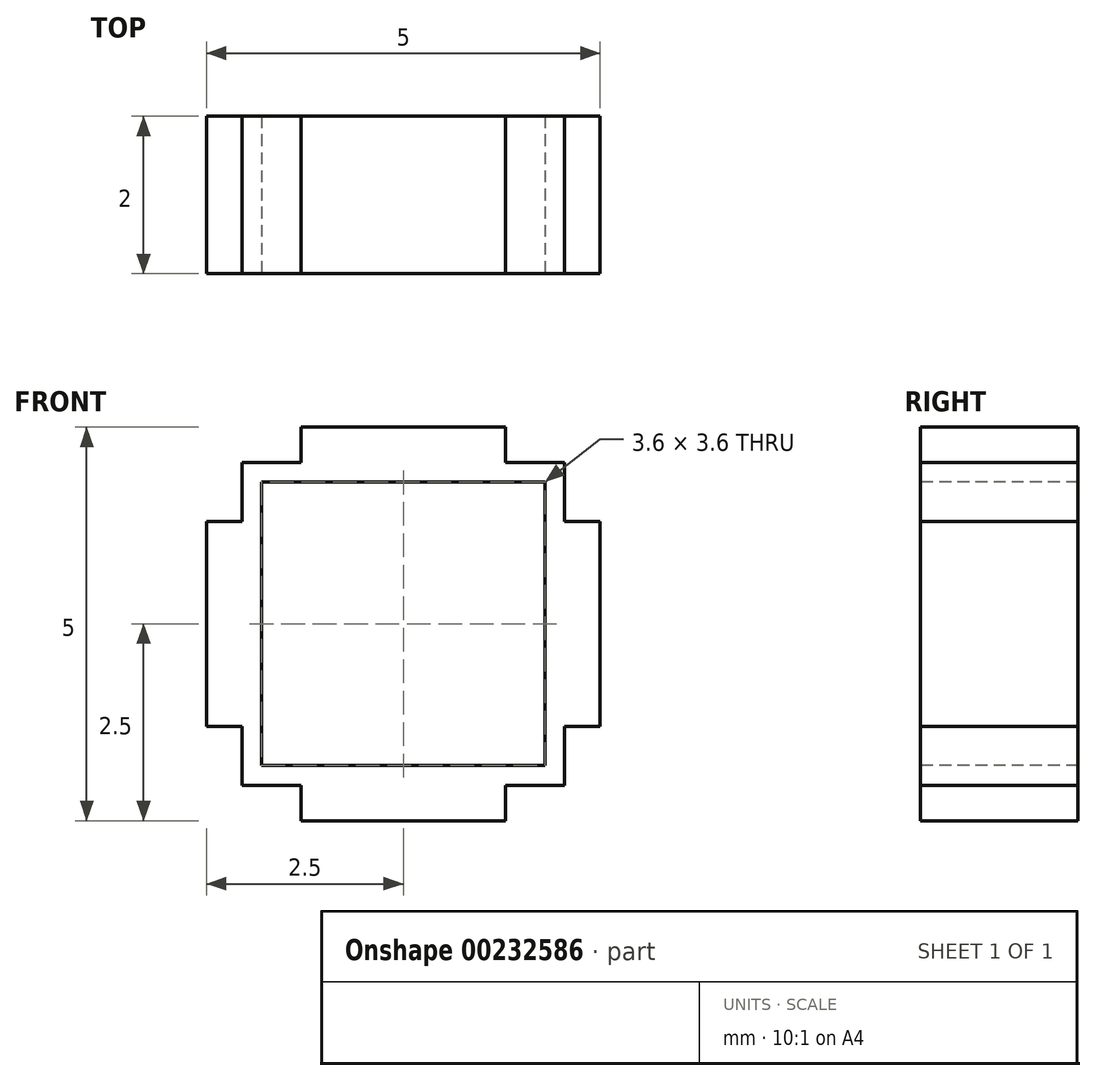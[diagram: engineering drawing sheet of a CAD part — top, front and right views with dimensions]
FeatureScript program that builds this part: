
annotation { "Feature Type Name" : "Feature", "Feature Type Description" : "" }
export const myFeature = defineFeature(function(context is Context, id is Id, definition is map)
    precondition{}
    {
        {
            var Q0;
            Q0=qCreatedBy(makeId("Front.planeOp"),FACE);
            var sketch = newSketch(context, id + "F0", { "sketchPlane" : qUnion([Q0])});
            skLineSegment(sketch, "E0.bottom", {"start": v(2.05, 2.05) * mm, "end": v(-2.05, 2.05) * mm});
            skLineSegment(sketch, "E0.top", {"start": v(2.05, -2.05) * mm, "end": v(-2.05, -2.05) * mm});
            skLineSegment(sketch, "E0.left", {"start": v(2.05, 2.05) * mm, "end": v(2.05, -2.05) * mm});
            skLineSegment(sketch, "E0.right", {"start": v(-2.05, 2.05) * mm, "end": v(-2.05, -2.05) * mm});
            skPoint(sketch, "E0.middle", {"position": v(0, 0) * mm});
            skSolve(sketch);
        }
        {
            var Q0;
            Q0 = qSketchRegion(id + "F0", true);
            extrude(context, id + "F1", {"entities" : qUnion([Q0]), "depth" : 2 * mm});
        }
        {
            var Q0;
            Q0=makeQuery(id+"F1.opExtrude","SWEPT_FACE",FACE,{"disambiguationData":[OSD([sQuery(id+"F0.wireOp",EDGE,"E0.top")])]});
            var sketch = newSketch(context, id + "F2", { "sketchPlane" : qUnion([Q0])});
            skLineSegment(sketch, "E1", {"start": v(-2.05, 2) * mm, "end": v(-1.3, 2) * mm});
            skLineSegment(sketch, "E2.bottom", {"start": v(-1.3, 2) * mm, "end": v(1.3, 2) * mm});
            skLineSegment(sketch, "E2.top", {"start": v(-1.3, 0) * mm, "end": v(1.3, 0) * mm});
            skLineSegment(sketch, "E2.left", {"start": v(-1.3, 2) * mm, "end": v(-1.3, 0) * mm});
            skLineSegment(sketch, "E2.right", {"start": v(1.3, 2) * mm, "end": v(1.3, 0) * mm});
            skSolve(sketch);
        }
        {
            var Q0;
            Q0 = qSketchRegion(id + "F2", true);
            extrude(context, id + "F3", {"entities" : qUnion([Q0]), "operationType" : NewBodyOperationType.ADD, "depth" : 0.45 * mm});
        }
        {
            var Q0;
            Q0=makeQuery(id+"F1.opExtrude","SWEPT_FACE",FACE,{"disambiguationData":[OSD([sQuery(id+"F0.wireOp",EDGE,"E0.right")])]});
            var sketch = newSketch(context, id + "F4", { "sketchPlane" : qUnion([Q0])});
            skLineSegment(sketch, "E3", {"start": v(2, 2.05) * mm, "end": v(2, 1.3) * mm});
            skLineSegment(sketch, "E4.bottom", {"start": v(2, 1.3) * mm, "end": v(0, 1.3) * mm});
            skLineSegment(sketch, "E4.top", {"start": v(2, -1.3) * mm, "end": v(0, -1.3) * mm});
            skLineSegment(sketch, "E4.left", {"start": v(2, 1.3) * mm, "end": v(2, -1.3) * mm});
            skLineSegment(sketch, "E4.right", {"start": v(0, 1.3) * mm, "end": v(0, -1.3) * mm});
            skSolve(sketch);
        }
        {
            var Q0;
            Q0 = qSketchRegion(id + "F4", true);
            extrude(context, id + "F5", {"entities" : qUnion([Q0]), "operationType" : NewBodyOperationType.ADD, "depth" : 0.45 * mm});
        }
        {
            var Q0;
            Q0=makeQuery(id+"F1.opExtrude","SWEPT_FACE",FACE,{"disambiguationData":[OSD([sQuery(id+"F0.wireOp",EDGE,"E0.bottom")])]});
            var sketch = newSketch(context, id + "F6", { "sketchPlane" : qUnion([Q0])});
            skLineSegment(sketch, "E5", {"start": v(2.05, -2) * mm, "end": v(1.3, -2) * mm});
            skLineSegment(sketch, "E6.bottom", {"start": v(1.3, -2) * mm, "end": v(-1.3, -2) * mm});
            skLineSegment(sketch, "E6.top", {"start": v(1.3, 0) * mm, "end": v(-1.3, 0) * mm});
            skLineSegment(sketch, "E6.left", {"start": v(1.3, -2) * mm, "end": v(1.3, 0) * mm});
            skLineSegment(sketch, "E6.right", {"start": v(-1.3, -2) * mm, "end": v(-1.3, 0) * mm});
            skSolve(sketch);
        }
        {
            var Q0;
            Q0 = qSketchRegion(id + "F6", true);
            extrude(context, id + "F7", {"entities" : qUnion([Q0]), "operationType" : NewBodyOperationType.ADD, "depth" : 0.45 * mm});
        }
        {
            var Q0;
            Q0=makeQuery(id+"F1.opExtrude","SWEPT_FACE",FACE,{"disambiguationData":[OSD([sQuery(id+"F0.wireOp",EDGE,"E0.left")])]});
            var sketch = newSketch(context, id + "F8", { "sketchPlane" : qUnion([Q0])});
            skLineSegment(sketch, "E7", {"start": v(-2, -2.05) * mm, "end": v(-2, -1.3) * mm});
            skLineSegment(sketch, "E8.bottom", {"start": v(-2, -1.3) * mm, "end": v(0, -1.3) * mm});
            skLineSegment(sketch, "E8.top", {"start": v(-2, 1.3) * mm, "end": v(0, 1.3) * mm});
            skLineSegment(sketch, "E8.left", {"start": v(-2, -1.3) * mm, "end": v(-2, 1.3) * mm});
            skLineSegment(sketch, "E8.right", {"start": v(0, -1.3) * mm, "end": v(0, 1.3) * mm});
            skSolve(sketch);
        }
        {
            var Q0;
            Q0 = qSketchRegion(id + "F8", true);
            extrude(context, id + "F9", {"entities" : qUnion([Q0]), "operationType" : NewBodyOperationType.ADD, "depth" : 0.45 * mm});
        }
        {
            var Q0;
            Q0=makeQuery(id+"F9.boolean.opBoolean","MERGE",FACE,{"derivedFrom":[makeQuery(id+"F7.boolean.opBoolean","MERGE",FACE,{"derivedFrom":[makeQuery(id+"F5.boolean.opBoolean","MERGE",FACE,{"derivedFrom":[makeQuery(id+"F3.boolean.opBoolean","MERGE",FACE,{"derivedFrom":[makeQuery(id+"F1.opExtrude","CAP_FACE",FACE,{"disambiguationData":[OSD([sQuery(id+"F0.wireOp",EDGE,"E0.bottom"),sQuery(id+"F0.wireOp",EDGE,"E0.top"),sQuery(id+"F0.wireOp",EDGE,"E0.left"),sQuery(id+"F0.wireOp",EDGE,"E0.right")])],"isStart":false}),makeQuery(id+"F3.opExtrude","SWEPT_FACE",FACE,{"disambiguationData":[OSD([sQuery(id+"F2.wireOp",EDGE,"E2.bottom")])]})]}),makeQuery(id+"F5.opExtrude","SWEPT_FACE",FACE,{"disambiguationData":[OSD([sQuery(id+"F4.wireOp",EDGE,"E4.left")])]})]}),makeQuery(id+"F7.opExtrude","SWEPT_FACE",FACE,{"disambiguationData":[OSD([sQuery(id+"F6.wireOp",EDGE,"E6.bottom")])]})]}),makeQuery(id+"F9.opExtrude","SWEPT_FACE",FACE,{"disambiguationData":[OSD([sQuery(id+"F8.wireOp",EDGE,"E8.left")])]})]});
            var sketch = newSketch(context, id + "F10", { "sketchPlane" : qUnion([Q0])});
            skLineSegment(sketch, "E9", {"start": v(2.5, 0) * mm, "end": v(-2.5, 0) * mm});
            skLineSegment(sketch, "E10", {"start": v(0, -2.5) * mm, "end": v(0, 2.5) * mm});
            skPoint(sketch, "E11", {"position": v(0, 0) * mm});
            skLineSegment(sketch, "E12.bottom", {"start": v(-1.8, -1.8) * mm, "end": v(1.8, -1.8) * mm});
            skLineSegment(sketch, "E12.top", {"start": v(-1.8, 1.8) * mm, "end": v(1.8, 1.8) * mm});
            skLineSegment(sketch, "E12.left", {"start": v(-1.8, -1.8) * mm, "end": v(-1.8, 1.8) * mm});
            skLineSegment(sketch, "E12.right", {"start": v(1.8, -1.8) * mm, "end": v(1.8, 1.8) * mm});
            skSolve(sketch);
        }
        {
            var Q0;
            Q0 = qSketchRegion(id + "F10", true);
            extrude(context, id + "F11", {"entities" : qUnion([Q0]), "operationType" : NewBodyOperationType.REMOVE, "oppositeDirection" : true, "depth" : 2 * mm});
        }
    });
